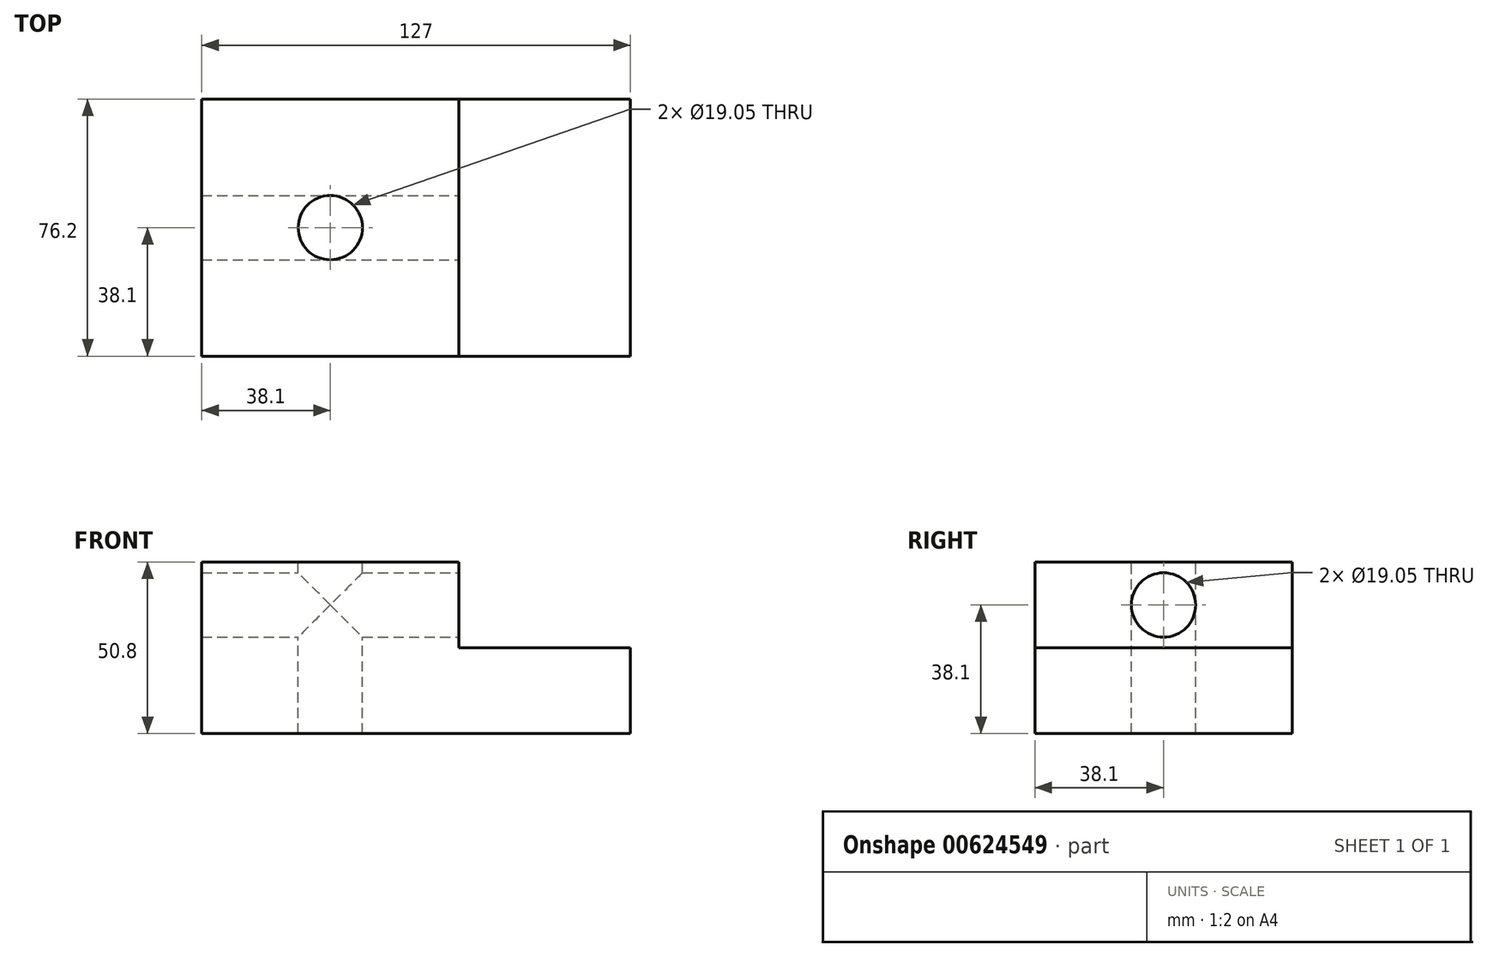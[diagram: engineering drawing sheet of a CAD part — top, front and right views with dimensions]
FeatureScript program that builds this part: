
annotation { "Feature Type Name" : "Feature", "Feature Type Description" : "" }
export const myFeature = defineFeature(function(context is Context, id is Id, definition is map)
    precondition{}
    {
        {
            var Q0;
            Q0=qCreatedBy(makeId("Front.planeOp"),FACE);
            var sketch = newSketch(context, id + "F0", { "sketchPlane" : qUnion([Q0])});
            skLineSegment(sketch, "E0.bottom", {"start": v(0, 0) * mm, "end": v(127, 0) * mm});
            skLineSegment(sketch, "E0.top", {"start": v(0, 50.8) * mm, "end": v(127, 50.8) * mm});
            skLineSegment(sketch, "E0.left", {"start": v(0, 0) * mm, "end": v(0, 50.8) * mm});
            skLineSegment(sketch, "E0.right", {"start": v(127, 0) * mm, "end": v(127, 50.8) * mm});
            skLineSegment(sketch, "E1", {"start": v(127, 25.4) * mm, "end": v(76.2, 25.4) * mm});
            skLineSegment(sketch, "E2", {"start": v(76.2, 25.4) * mm, "end": v(76.2, 50.8) * mm});
            skSolve(sketch);
        }
        {
            var Q0;
            {var subQ1=sQuery(id+"F0.wireOp",EDGE,"E0.bottom");Q0=makeQuery(id+"F0.imprint","IMPRINT",FACE,{"disambiguationData":[TD([[makeQuery(id+"F0.imprint","IMPRINT",EDGE,{"derivedFrom":subQ1}),1.0]])]});}
            extrude(context, id + "F1", {"entities" : qUnion([Q0]), "depth" : 76.2 * mm, "offsetDistance" : 25.4 * mm});
        }
        {
            var Q0;
            Q0=makeQuery(id+"F1.opExtrude","SWEPT_FACE",FACE,{"disambiguationData":[OSD([sQuery(id+"F0.wireOp",EDGE,"E0.top")])]});
            var sketch = newSketch(context, id + "F2", { "sketchPlane" : qUnion([Q0])});
            skPoint(sketch, "E3", {"position": v(38.1, -38.1) * mm});
            skPoint(sketch, "E3.positionSnap0", {"position": v(38.1, 0) * mm});
            skPoint(sketch, "E3.positionSnap1", {"position": v(0, -38.1) * mm});
            skSolve(sketch);
        }
        {
            var Q0;
            Q0=sQuery(id+"F2.wireOp",VERTEX,"E3");
            var Q1;
            Q1=makeQuery(id+"F1.opExtrude","SWEPT_BODY",BODY,{"disambiguationData":[OSD([sQuery(id+"F0.wireOp",EDGE,"E0.bottom"),sQuery(id+"F0.wireOp",EDGE,"E0.top"),sQuery(id+"F0.wireOp",EDGE,"E0.left"),sQuery(id+"F0.wireOp",EDGE,"E0.right"),sQuery(id+"F0.wireOp",EDGE,"E1"),sQuery(id+"F0.wireOp",EDGE,"E2")])]});
            hole(context, id + "F3", {"style" : HoleStyle.SIMPLE, "endStyle" : HoleEndStyle.THROUGH, "holeDiameter" : 19.05 * mm, "majorDiameter" : 6.35 * mm, "isTappedThrough" : true, "tappedDepth" : 12.7 * mm, "tapClearance" : 3, "locations" : qUnion([Q0]), "scope" : qUnion([Q1])});
        }
        {
            var Q0;
            Q0=makeQuery(id+"F1.opExtrude","SWEPT_FACE",FACE,{"disambiguationData":[OSD([sQuery(id+"F0.wireOp",EDGE,"E2")])]});
            var sketch = newSketch(context, id + "F4", { "sketchPlane" : qUnion([Q0])});
            skPoint(sketch, "E4", {"position": v(-38.1, 38.1) * mm});
            skPoint(sketch, "E4.positionSnap0", {"position": v(-76.2, 38.1) * mm});
            skPoint(sketch, "E4.positionSnap1", {"position": v(-38.1, 50.8) * mm});
            skSolve(sketch);
        }
        {
            var Q0;
            Q0=sQuery(id+"F4.wireOp",VERTEX,"E4");
            var Q1;
            Q1=makeQuery(id+"F1.opExtrude","SWEPT_BODY",BODY,{"disambiguationData":[OSD([sQuery(id+"F0.wireOp",EDGE,"E0.bottom"),sQuery(id+"F0.wireOp",EDGE,"E0.top"),sQuery(id+"F0.wireOp",EDGE,"E0.left"),sQuery(id+"F0.wireOp",EDGE,"E0.right"),sQuery(id+"F0.wireOp",EDGE,"E1"),sQuery(id+"F0.wireOp",EDGE,"E2")])]});
            hole(context, id + "F5", {"style" : HoleStyle.SIMPLE, "endStyle" : HoleEndStyle.THROUGH, "holeDiameter" : 19.05 * mm, "majorDiameter" : 6.35 * mm, "isTappedThrough" : true, "tappedDepth" : 12.7 * mm, "tapClearance" : 3, "locations" : qUnion([Q0]), "scope" : qUnion([Q1])});
        }
    });
